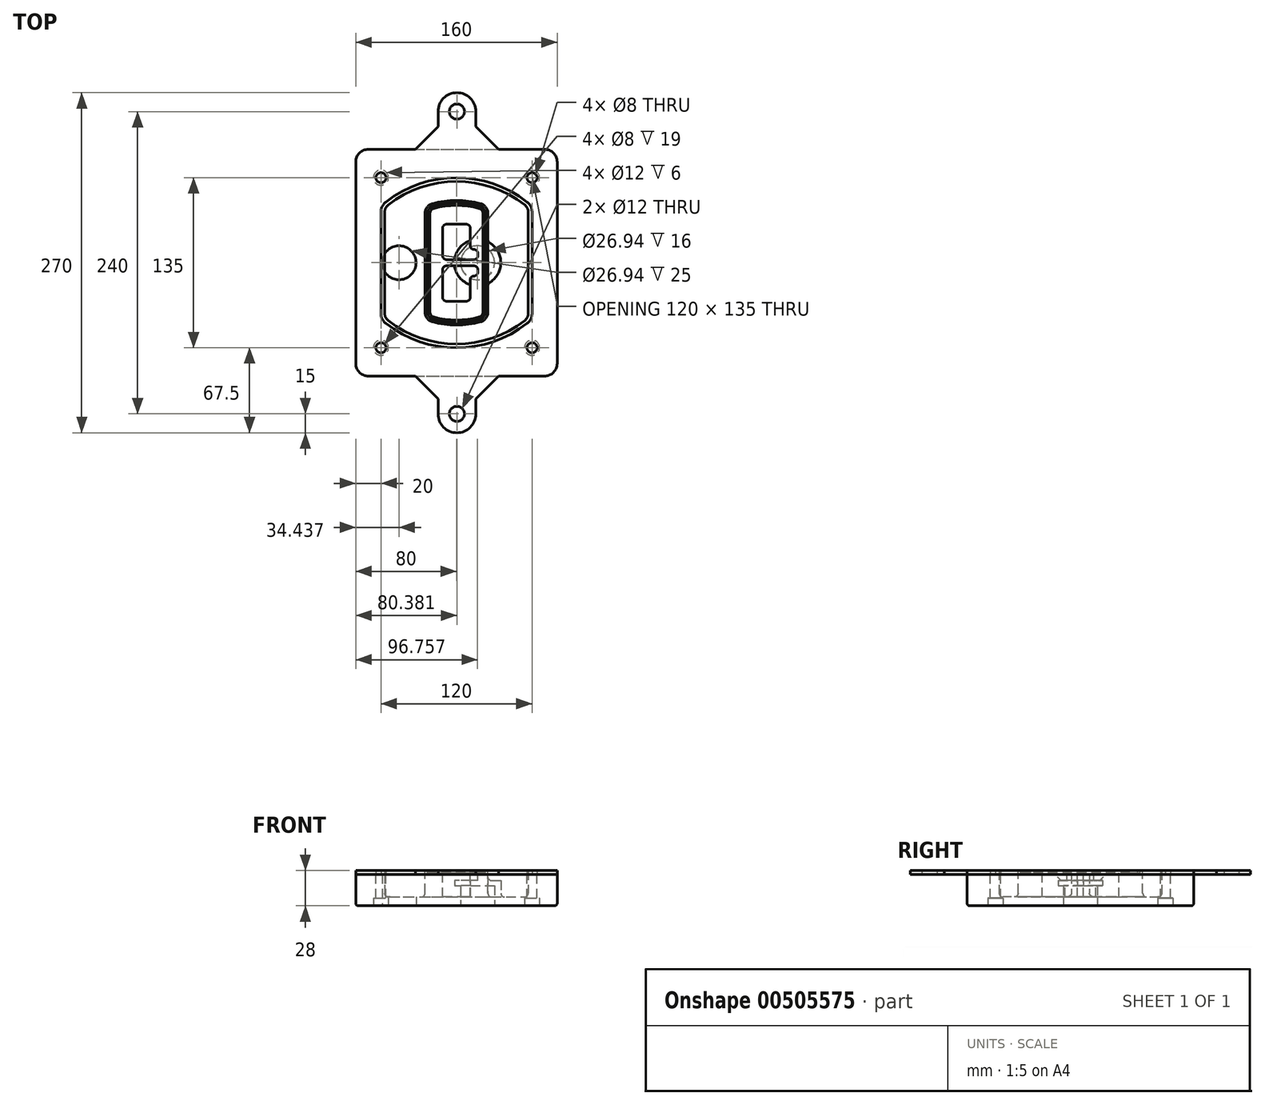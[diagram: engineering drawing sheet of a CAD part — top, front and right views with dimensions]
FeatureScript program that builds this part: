
annotation { "Feature Type Name" : "Feature", "Feature Type Description" : "" }
export const myFeature = defineFeature(function(context is Context, id is Id, definition is map)
    precondition{}
    {
        {
            var Q0;
            Q0=qCreatedBy(makeId("Top.planeOp"),FACE);
            var sketch = newSketch(context, id + "F0", { "sketchPlane" : qUnion([Q0])});
            skPoint(sketch, "E0.rect.middle", {"position": v(0, 0) * mm});
            skLineSegment(sketch, "E1.bottom", {"start": v(-70, -90) * mm, "end": v(70, -90) * mm});
            skLineSegment(sketch, "E1.top", {"start": v(-70, 90) * mm, "end": v(70, 90) * mm});
            skLineSegment(sketch, "E1.left", {"start": v(-80, -80) * mm, "end": v(-80, 80) * mm});
            skLineSegment(sketch, "E1.right", {"start": v(80, -80) * mm, "end": v(80, 80) * mm});
            skLineSegment(sketch, "E2", {"start": v(-80, 90) * mm, "end": v(80, -90) * mm, "construction": true});
            skLineSegment(sketch, "E3", {"start": v(80, 90) * mm, "end": v(-80, -90) * mm, "construction": true});
            skCircle(sketch, "E4", {"center": v(-60, 67.5) * mm, "radius": 4 * mm});
            skCircle(sketch, "E5", {"center": v(60, 67.5) * mm, "radius": 4 * mm});
            skCircle(sketch, "E6", {"center": v(60, -67.5) * mm, "radius": 4 * mm});
            skCircle(sketch, "E7", {"center": v(-60, -67.5) * mm, "radius": 4 * mm});
            skLineSegment(sketch, "E8", {"start": v(-60, 67.5) * mm, "end": v(60, 67.5) * mm, "construction": true});
            skLineSegment(sketch, "E9", {"start": v(60, 67.5) * mm, "end": v(60, -67.5) * mm, "construction": true});
            skLineSegment(sketch, "E10", {"start": v(60, -67.5) * mm, "end": v(-60, -67.5) * mm, "construction": true});
            skLineSegment(sketch, "E11", {"start": v(-60, -67.5) * mm, "end": v(-60, 67.5) * mm, "construction": true});
            skLineSegment(sketch, "E12", {"start": v(-60, 40.3) * mm, "end": v(-60, -40.3) * mm});
            skLineSegment(sketch, "E13", {"start": v(60, 40.3) * mm, "end": v(60, -40.3) * mm});
            skArc(sketch, "E14", {"start": v(56.15, 48.18) * mm, "mid": v(0, 67.5) * mm, "end": v(-56.15, 48.18) * mm});
            skArc(sketch, "E15", {"start": v(-56.15, -48.18) * mm, "mid": v(0, -67.5) * mm, "end": v(56.15, -48.18) * mm});
            skLineSegment(sketch, "E16", {"start": v(-60, 0) * mm, "end": v(60, 0) * mm, "construction": true});
            skPoint(sketch, "E17.visualSharp", {"position": v(-60, -45) * mm});
            skArc(sketch, "E17.filletArc", {"start": v(-60, -40.3) * mm, "mid": v(-58.99, -44.68) * mm, "end": v(-56.15, -48.18) * mm});
            skPoint(sketch, "E18.visualSharp", {"position": v(-60, 45) * mm});
            skArc(sketch, "E18.filletArc", {"start": v(-56.15, 48.18) * mm, "mid": v(-58.99, 44.68) * mm, "end": v(-60, 40.3) * mm});
            skPoint(sketch, "E19.visualSharp", {"position": v(60, 45) * mm});
            skArc(sketch, "E19.filletArc", {"start": v(60, 40.3) * mm, "mid": v(58.99, 44.68) * mm, "end": v(56.15, 48.18) * mm});
            skPoint(sketch, "E20.visualSharp", {"position": v(60, -45) * mm});
            skArc(sketch, "E20.filletArc", {"start": v(56.15, -48.18) * mm, "mid": v(58.99, -44.68) * mm, "end": v(60, -40.3) * mm});
            skPoint(sketch, "E21.visualSharp", {"position": v(-80, 90) * mm});
            skArc(sketch, "E21.filletArc", {"start": v(-70, 90) * mm, "mid": v(-77.07, 87.07) * mm, "end": v(-80, 80) * mm});
            skPoint(sketch, "E22.visualSharp", {"position": v(80, 90) * mm});
            skArc(sketch, "E22.filletArc", {"start": v(80, 80) * mm, "mid": v(77.07, 87.07) * mm, "end": v(70, 90) * mm});
            skPoint(sketch, "E23.visualSharp", {"position": v(80, -90) * mm});
            skArc(sketch, "E23.filletArc", {"start": v(70, -90) * mm, "mid": v(77.07, -87.07) * mm, "end": v(80, -80) * mm});
            skPoint(sketch, "E24.visualSharp", {"position": v(-80, -90) * mm});
            skArc(sketch, "E24.filletArc", {"start": v(-80, -80) * mm, "mid": v(-77.07, -87.07) * mm, "end": v(-70, -90) * mm});
            skArc(sketch, "E25.0", {"start": v(57, 40.3) * mm, "mid": v(56.3, 43.36) * mm, "end": v(54.3, 45.81) * mm});
            skLineSegment(sketch, "E25.1", {"start": v(57, 40.3) * mm, "end": v(57, -40.3) * mm});
            skArc(sketch, "E25.2", {"start": v(54.3, -45.81) * mm, "mid": v(56.3, -43.36) * mm, "end": v(57, -40.3) * mm});
            skArc(sketch, "E25.3", {"start": v(-54.3, -45.81) * mm, "mid": v(0, -64.5) * mm, "end": v(54.3, -45.81) * mm});
            skArc(sketch, "E25.4", {"start": v(-57, -40.3) * mm, "mid": v(-56.3, -43.36) * mm, "end": v(-54.3, -45.81) * mm});
            skArc(sketch, "E25.5", {"start": v(54.3, 45.81) * mm, "mid": v(0, 64.5) * mm, "end": v(-54.3, 45.81) * mm});
            skLineSegment(sketch, "E25.6", {"start": v(-57, 40.3) * mm, "end": v(-57, -40.3) * mm});
            skArc(sketch, "E25.7", {"start": v(-54.3, 45.81) * mm, "mid": v(-56.3, 43.36) * mm, "end": v(-57, 40.3) * mm});
            skArc(sketch, "E26.0", {"start": v(-58.62, 51.33) * mm, "mid": v(-62.58, 46.43) * mm, "end": v(-64, 40.3) * mm});
            skArc(sketch, "E26.1", {"start": v(58.62, 51.33) * mm, "mid": v(0, 71.5) * mm, "end": v(-58.62, 51.33) * mm});
            skArc(sketch, "E26.2", {"start": v(64, 40.3) * mm, "mid": v(62.58, 46.43) * mm, "end": v(58.62, 51.33) * mm});
            skLineSegment(sketch, "E26.3", {"start": v(64, 40.3) * mm, "end": v(64, -40.3) * mm});
            skArc(sketch, "E26.4", {"start": v(58.62, -51.33) * mm, "mid": v(62.58, -46.43) * mm, "end": v(64, -40.3) * mm});
            skLineSegment(sketch, "E26.5", {"start": v(-64, 40.3) * mm, "end": v(-64, -40.3) * mm});
            skArc(sketch, "E26.6", {"start": v(-58.62, -51.33) * mm, "mid": v(0, -71.5) * mm, "end": v(58.62, -51.33) * mm});
            skArc(sketch, "E26.7", {"start": v(-64, -40.3) * mm, "mid": v(-62.58, -46.43) * mm, "end": v(-58.62, -51.33) * mm});
            skSolve(sketch);
        }
        {
            var Q0;
            Q0=makeQuery(id+"F0.imprint","IMPRINT",FACE,{"disambiguationData":[TD([[makeQuery(id+"F0.imprint","IMPRINT",EDGE,{"derivedFrom":sQuery(id+"F0.wireOp",EDGE,"E1.bottom")}),1.0]])]});
            var Q1;
            Q1=makeQuery(id+"F0.imprint","IMPRINT",FACE,{"disambiguationData":[TD([[makeQuery(id+"F0.imprint","IMPRINT",EDGE,{"derivedFrom":sQuery(id+"F0.wireOp",EDGE,"E12")}),1.0]])]});
            var Q2;
            Q2=makeQuery(id+"F0.imprint","IMPRINT",FACE,{"disambiguationData":[TD([[makeQuery(id+"F0.imprint","IMPRINT",EDGE,{"derivedFrom":sQuery(id+"F0.wireOp",EDGE,"E25.0")}),1.0]])]});
            var Q3;
            Q3=makeQuery(id+"F0.imprint","IMPRINT",FACE,{"disambiguationData":[TD([[makeQuery(id+"F0.imprint","IMPRINT",EDGE,{"derivedFrom":sQuery(id+"F0.wireOp",EDGE,"E12")}),-1.0]])]});
            extrude(context, id + "F1", {"entities" : qUnion([Q0, Q1, Q2, Q3]), "oppositeDirection" : true, "depth" : 25 * mm});
        }
        {
            var Q0;
            Q0=makeQuery(id+"F0.imprint","IMPRINT",FACE,{"disambiguationData":[TD([[makeQuery(id+"F0.imprint","IMPRINT",EDGE,{"derivedFrom":sQuery(id+"F0.wireOp",EDGE,"E12")}),1.0]])]});
            extrude(context, id + "F2", {"entities" : qUnion([Q0]), "operationType" : NewBodyOperationType.ADD, "depth" : 3 * mm});
        }
        {
            var Q0;
            Q0=makeQuery(id+"F0.imprint","IMPRINT",FACE,{"disambiguationData":[TD([[makeQuery(id+"F0.imprint","IMPRINT",EDGE,{"derivedFrom":sQuery(id+"F0.wireOp",EDGE,"E25.0")}),1.0]])]});
            extrude(context, id + "F3", {"entities" : qUnion([Q0]), "operationType" : NewBodyOperationType.REMOVE, "oppositeDirection" : true, "depth" : 18 * mm});
        }
        {
            var Q0;
            Q0=makeQuery(id+"F2.opExtrude","CAP_FACE",FACE,{"disambiguationData":[OSD([sQuery(id+"F0.wireOp",EDGE,"E12"),sQuery(id+"F0.wireOp",EDGE,"E13"),sQuery(id+"F0.wireOp",EDGE,"E14"),sQuery(id+"F0.wireOp",EDGE,"E15"),sQuery(id+"F0.wireOp",EDGE,"E17.filletArc"),sQuery(id+"F0.wireOp",EDGE,"E18.filletArc"),sQuery(id+"F0.wireOp",EDGE,"E19.filletArc"),sQuery(id+"F0.wireOp",EDGE,"E20.filletArc"),sQuery(id+"F0.wireOp",EDGE,"E25.0"),sQuery(id+"F0.wireOp",EDGE,"E25.1"),sQuery(id+"F0.wireOp",EDGE,"E25.2"),sQuery(id+"F0.wireOp",EDGE,"E25.3"),sQuery(id+"F0.wireOp",EDGE,"E25.4"),sQuery(id+"F0.wireOp",EDGE,"E25.5"),sQuery(id+"F0.wireOp",EDGE,"E25.6"),sQuery(id+"F0.wireOp",EDGE,"E25.7")])],"isStart":false});
            var sketch = newSketch(context, id + "F4", { "sketchPlane" : qUnion([Q0])});
            skArc(sketch, "E27.0", {"start": v(-19.08, -46.97) * mm, "mid": v(0, -49.5) * mm, "end": v(19.08, -46.97) * mm});
            skArc(sketch, "E28.0", {"start": v(19.08, 46.97) * mm, "mid": v(0, 49.5) * mm, "end": v(-19.08, 46.97) * mm});
            skLineSegment(sketch, "E29", {"start": v(-25, 39.25) * mm, "end": v(-25, -39.25) * mm});
            skLineSegment(sketch, "E30", {"start": v(25, 39.25) * mm, "end": v(25, -39.25) * mm});
            skLineSegment(sketch, "E31", {"start": v(-25, 45.1) * mm, "end": v(25, 45.1) * mm, "construction": true});
            skLineSegment(sketch, "E32", {"start": v(-25, -45.1) * mm, "end": v(25, -45.1) * mm, "construction": true});
            skPoint(sketch, "E33.visualSharp", {"position": v(-25, 45.1) * mm});
            skArc(sketch, "E33.filletArc", {"start": v(-19.08, 46.97) * mm, "mid": v(-23.35, 44.11) * mm, "end": v(-25, 39.25) * mm});
            skPoint(sketch, "E34.visualSharp", {"position": v(25, 45.1) * mm});
            skArc(sketch, "E34.filletArc", {"start": v(25, 39.25) * mm, "mid": v(23.35, 44.11) * mm, "end": v(19.08, 46.97) * mm});
            skPoint(sketch, "E35.visualSharp", {"position": v(25, -45.1) * mm});
            skArc(sketch, "E35.filletArc", {"start": v(19.08, -46.97) * mm, "mid": v(23.35, -44.11) * mm, "end": v(25, -39.25) * mm});
            skPoint(sketch, "E36.visualSharp", {"position": v(-25, -45.1) * mm});
            skArc(sketch, "E36.filletArc", {"start": v(-25, -39.25) * mm, "mid": v(-23.35, -44.11) * mm, "end": v(-19.08, -46.97) * mm});
            skArc(sketch, "E37.0", {"start": v(54.3, 45.81) * mm, "mid": v(0, 64.5) * mm, "end": v(-54.3, 45.81) * mm});
            skArc(sketch, "E37.1", {"start": v(-54.3, 45.81) * mm, "mid": v(-56.3, 43.36) * mm, "end": v(-57, 40.3) * mm});
            skLineSegment(sketch, "E37.2", {"start": v(-57, 40.3) * mm, "end": v(-57, -40.3) * mm});
            skArc(sketch, "E37.3", {"start": v(-57, -40.3) * mm, "mid": v(-56.3, -43.36) * mm, "end": v(-54.3, -45.81) * mm});
            skArc(sketch, "E37.4", {"start": v(-54.3, -45.81) * mm, "mid": v(0, -64.5) * mm, "end": v(54.3, -45.81) * mm});
            skArc(sketch, "E37.5", {"start": v(54.3, -45.81) * mm, "mid": v(56.3, -43.36) * mm, "end": v(57, -40.3) * mm});
            skLineSegment(sketch, "E37.6", {"start": v(57, 40.3) * mm, "end": v(57, -40.3) * mm});
            skArc(sketch, "E37.7", {"start": v(57, 40.3) * mm, "mid": v(56.3, 43.36) * mm, "end": v(54.3, 45.81) * mm});
            skLineSegment(sketch, "E38.0", {"start": v(23, 39.25) * mm, "end": v(23, -39.25) * mm});
            skArc(sketch, "E38.1", {"start": v(18.56, -45.04) * mm, "mid": v(21.76, -42.9) * mm, "end": v(23, -39.25) * mm});
            skArc(sketch, "E38.2", {"start": v(-18.56, -45.04) * mm, "mid": v(0, -47.5) * mm, "end": v(18.56, -45.04) * mm});
            skArc(sketch, "E38.3", {"start": v(-23, -39.25) * mm, "mid": v(-21.76, -42.9) * mm, "end": v(-18.56, -45.04) * mm});
            skLineSegment(sketch, "E38.4", {"start": v(-23, 39.25) * mm, "end": v(-23, -39.25) * mm});
            skArc(sketch, "E38.5", {"start": v(23, 39.25) * mm, "mid": v(21.76, 42.9) * mm, "end": v(18.56, 45.04) * mm});
            skArc(sketch, "E38.6", {"start": v(-18.56, 45.04) * mm, "mid": v(-21.76, 42.9) * mm, "end": v(-23, 39.25) * mm});
            skArc(sketch, "E38.7", {"start": v(18.56, 45.04) * mm, "mid": v(0, 47.5) * mm, "end": v(-18.56, 45.04) * mm});
            skArc(sketch, "E39.0", {"start": v(21, 39.25) * mm, "mid": v(20.18, 41.68) * mm, "end": v(18.04, 43.1) * mm});
            skLineSegment(sketch, "E39.1", {"start": v(21, 39.25) * mm, "end": v(21, -39.25) * mm});
            skArc(sketch, "E39.2", {"start": v(18.04, -43.1) * mm, "mid": v(20.18, -41.68) * mm, "end": v(21, -39.25) * mm});
            skArc(sketch, "E39.3", {"start": v(-18.04, -43.1) * mm, "mid": v(0, -45.5) * mm, "end": v(18.04, -43.1) * mm});
            skArc(sketch, "E39.4", {"start": v(-21, -39.25) * mm, "mid": v(-20.18, -41.68) * mm, "end": v(-18.04, -43.1) * mm});
            skArc(sketch, "E39.5", {"start": v(18.04, 43.1) * mm, "mid": v(0, 45.5) * mm, "end": v(-18.04, 43.1) * mm});
            skLineSegment(sketch, "E39.6", {"start": v(-21, 39.25) * mm, "end": v(-21, -39.25) * mm});
            skArc(sketch, "E39.7", {"start": v(-18.04, 43.1) * mm, "mid": v(-20.18, 41.68) * mm, "end": v(-21, 39.25) * mm});
            skLineSegment(sketch, "E40", {"start": v(-25, 0) * mm, "end": v(25, 0) * mm, "construction": true});
            skLineSegment(sketch, "E41", {"start": v(-11, 5.5) * mm, "end": v(-11, 27.5) * mm});
            skLineSegment(sketch, "E42", {"start": v(-8, 30.5) * mm, "end": v(8, 30.5) * mm});
            skLineSegment(sketch, "E43", {"start": v(11, 27.5) * mm, "end": v(11, 13.5) * mm});
            skLineSegment(sketch, "E44", {"start": v(14, 10.5) * mm, "end": v(14, 10.5) * mm});
            skLineSegment(sketch, "E45", {"start": v(17, 7.5) * mm, "end": v(17, 5.5) * mm});
            skLineSegment(sketch, "E46", {"start": v(14, 2.5) * mm, "end": v(-8, 2.5) * mm});
            skPoint(sketch, "E47.visualSharp", {"position": v(-11, 30.5) * mm});
            skArc(sketch, "E47.filletArc", {"start": v(-8, 30.5) * mm, "mid": v(-10.12, 29.62) * mm, "end": v(-11, 27.5) * mm});
            skPoint(sketch, "E48.visualSharp", {"position": v(11, 30.5) * mm});
            skArc(sketch, "E48.filletArc", {"start": v(11, 27.5) * mm, "mid": v(10.12, 29.62) * mm, "end": v(8, 30.5) * mm});
            skPoint(sketch, "E49.visualSharp", {"position": v(11, 10.5) * mm});
            skArc(sketch, "E49.filletArc", {"start": v(11, 13.5) * mm, "mid": v(11.88, 11.38) * mm, "end": v(14, 10.5) * mm});
            skPoint(sketch, "E50.visualSharp", {"position": v(17, 10.5) * mm});
            skArc(sketch, "E50.filletArc", {"start": v(17, 7.5) * mm, "mid": v(16.12, 9.62) * mm, "end": v(14, 10.5) * mm});
            skPoint(sketch, "E51.visualSharp", {"position": v(17, 2.5) * mm});
            skArc(sketch, "E51.filletArc", {"start": v(14, 2.5) * mm, "mid": v(16.12, 3.38) * mm, "end": v(17, 5.5) * mm});
            skPoint(sketch, "E52.visualSharp", {"position": v(-11, 2.5) * mm});
            skArc(sketch, "E52.filletArc", {"start": v(-11, 5.5) * mm, "mid": v(-10.12, 3.38) * mm, "end": v(-8, 2.5) * mm});
            skLineSegment(sketch, "E53.0.MirrorCS", {"start": v(14, -2.5) * mm, "end": v(-8, -2.5) * mm});
            skArc(sketch, "E54.0.MirrorCS", {"start": v(-11, -5.5) * mm, "mid": v(-10.12, -3.38) * mm, "end": v(-8, -2.5) * mm});
            skLineSegment(sketch, "E55.0.MirrorCS", {"start": v(-11, -5.5) * mm, "end": v(-11, -27.5) * mm});
            skArc(sketch, "E56.0.MirrorCS", {"start": v(-8, -30.5) * mm, "mid": v(-10.12, -29.62) * mm, "end": v(-11, -27.5) * mm});
            skLineSegment(sketch, "E57.0.MirrorCS", {"start": v(-8, -30.5) * mm, "end": v(8, -30.5) * mm});
            skArc(sketch, "E58.0.MirrorCS", {"start": v(11, -27.5) * mm, "mid": v(10.12, -29.62) * mm, "end": v(8, -30.5) * mm});
            skLineSegment(sketch, "E59.0.MirrorCS", {"start": v(11, -27.5) * mm, "end": v(11, -13.5) * mm});
            skArc(sketch, "E60.0.MirrorCS", {"start": v(11, -13.5) * mm, "mid": v(11.88, -11.38) * mm, "end": v(14, -10.5) * mm});
            skArc(sketch, "E61.0.MirrorCS", {"start": v(17, -7.5) * mm, "mid": v(16.12, -9.62) * mm, "end": v(14, -10.5) * mm});
            skLineSegment(sketch, "E62.0.MirrorCS", {"start": v(17, -7.5) * mm, "end": v(17, -5.5) * mm});
            skArc(sketch, "E63.0.MirrorCS", {"start": v(14, -2.5) * mm, "mid": v(16.12, -3.38) * mm, "end": v(17, -5.5) * mm});
            skSolve(sketch);
        }
        {
            var Q0;
            Q0=makeQuery(id+"F4.imprint","IMPRINT",FACE,{"disambiguationData":[TD([[makeQuery(id+"F4.imprint","IMPRINT",EDGE,{"derivedFrom":sQuery(id+"F4.wireOp",EDGE,"E27.0")}),1.0]])]});
            var Q1;
            Q1=makeQuery(id+"F4.imprint","IMPRINT",FACE,{"disambiguationData":[TD([[makeQuery(id+"F4.imprint","IMPRINT",EDGE,{"derivedFrom":sQuery(id+"F4.wireOp",EDGE,"E38.0")}),-1.0]])]});
            var Q2;
            Q2=makeQuery(id+"F4.imprint","IMPRINT",FACE,{"disambiguationData":[TD([[makeQuery(id+"F4.imprint","IMPRINT",EDGE,{"derivedFrom":sQuery(id+"F4.wireOp",EDGE,"E39.0")}),1.0]])]});
            extrude(context, id + "F5", {"entities" : qUnion([Q0, Q1, Q2]), "operationType" : NewBodyOperationType.ADD, "endBound" : BoundingType.UP_TO_NEXT, "oppositeDirection" : true, "depth" : 25 * mm});
        }
        {
            var Q0;
            Q0=makeQuery(id+"F4.imprint","IMPRINT",FACE,{"disambiguationData":[TD([[makeQuery(id+"F4.imprint","IMPRINT",EDGE,{"derivedFrom":sQuery(id+"F4.wireOp",EDGE,"E38.0")}),-1.0]])]});
            extrude(context, id + "F6", {"entities" : qUnion([Q0]), "operationType" : NewBodyOperationType.REMOVE, "oppositeDirection" : true, "depth" : 2 * mm});
        }
        {
            var Q0;
            Q0=makeQuery(id+"F1.opExtrude","CAP_FACE",FACE,{"disambiguationData":[OSD([sQuery(id+"F0.wireOp",EDGE,"E1.bottom"),sQuery(id+"F0.wireOp",EDGE,"E1.top"),sQuery(id+"F0.wireOp",EDGE,"E1.left"),sQuery(id+"F0.wireOp",EDGE,"E1.right"),sQuery(id+"F0.wireOp",EDGE,"E4"),sQuery(id+"F0.wireOp",EDGE,"E5"),sQuery(id+"F0.wireOp",EDGE,"E6"),sQuery(id+"F0.wireOp",EDGE,"E7"),sQuery(id+"F0.wireOp",EDGE,"E21.filletArc"),sQuery(id+"F0.wireOp",EDGE,"E22.filletArc"),sQuery(id+"F0.wireOp",EDGE,"E23.filletArc"),sQuery(id+"F0.wireOp",EDGE,"E24.filletArc")])],"isStart":false});
            var sketch = newSketch(context, id + "F7", { "sketchPlane" : qUnion([Q0])});
            skCircle(sketch, "E64", {"center": v(16.76, 0) * mm, "radius": 13.47 * mm});
            skCircle(sketch, "E65", {"center": v(-45.56, 0) * mm, "radius": 13.47 * mm});
            skLineSegment(sketch, "E66", {"start": v(80, 0) * mm, "end": v(-80, 0) * mm});
            skCircle(sketch, "E67", {"center": v(16.76, 0) * mm, "radius": 18.47 * mm});
            skCircle(sketch, "E68", {"center": v(60, -67.5) * mm, "radius": 6 * mm});
            skCircle(sketch, "E69", {"center": v(-60, -67.5) * mm, "radius": 6 * mm});
            skCircle(sketch, "E70", {"center": v(-60, 67.5) * mm, "radius": 6 * mm});
            skCircle(sketch, "E71", {"center": v(60, 67.5) * mm, "radius": 6 * mm});
            skSolve(sketch);
        }
        {
            var Q0;
            {var subQ1=sQuery(id+"F7.wireOp",EDGE,"E66");var subQ4=sQuery(id+"F7.wireOp",EDGE,"E64");var subQ6=makeQuery(id+"F7.imprint","INTERSECT",VERTEX,{"disambiguationData":[OD(0.0)],"derivedFrom":[subQ4,subQ1]});Q0=makeQuery(id+"F7.imprint","IMPRINT",FACE,{"disambiguationData":[TD([[makeQuery(id+"F7.imprint","IMPRINT",EDGE,{"disambiguationData":[TD([[subQ6,-1.0]])],"derivedFrom":subQ4}),-1.0]])]});}
            var Q1;
            {var subQ0=sQuery(id+"F7.wireOp",EDGE,"E66");var subQ1=sQuery(id+"F7.wireOp",EDGE,"E64");var subQ3=makeQuery(id+"F7.imprint","INTERSECT",VERTEX,{"disambiguationData":[OD(0.0)],"derivedFrom":[subQ1,subQ0]});Q1=makeQuery(id+"F7.imprint","IMPRINT",FACE,{"disambiguationData":[TD([[makeQuery(id+"F7.imprint","IMPRINT",EDGE,{"disambiguationData":[TD([[subQ3,-1.0]])],"derivedFrom":subQ1}),1.0]])]});}
            var Q2;
            {var subQ0=sQuery(id+"F7.wireOp",EDGE,"E66");var subQ1=sQuery(id+"F7.wireOp",EDGE,"E64");var subQ3=makeQuery(id+"F7.imprint","INTERSECT",VERTEX,{"disambiguationData":[OD(0.0)],"derivedFrom":[subQ1,subQ0]});Q2=makeQuery(id+"F7.imprint","IMPRINT",FACE,{"disambiguationData":[TD([[makeQuery(id+"F7.imprint","IMPRINT",EDGE,{"disambiguationData":[TD([[subQ3,1.0]])],"derivedFrom":subQ1}),1.0]])]});}
            var Q3;
            {var subQ1=sQuery(id+"F7.wireOp",EDGE,"E66");var subQ4=sQuery(id+"F7.wireOp",EDGE,"E64");var subQ6=makeQuery(id+"F7.imprint","INTERSECT",VERTEX,{"disambiguationData":[OD(0.0)],"derivedFrom":[subQ4,subQ1]});Q3=makeQuery(id+"F7.imprint","IMPRINT",FACE,{"disambiguationData":[TD([[makeQuery(id+"F7.imprint","IMPRINT",EDGE,{"disambiguationData":[TD([[subQ6,1.0]])],"derivedFrom":subQ4}),-1.0]])]});}
            extrude(context, id + "F8", {"entities" : qUnion([Q0, Q1, Q2, Q3]), "operationType" : NewBodyOperationType.ADD, "oppositeDirection" : true, "depth" : 20 * mm});
        }
        {
            var Q0;
            {var subQ0=sQuery(id+"F7.wireOp",EDGE,"E66");var subQ1=sQuery(id+"F7.wireOp",EDGE,"E64");var subQ3=makeQuery(id+"F7.imprint","INTERSECT",VERTEX,{"disambiguationData":[OD(0.0)],"derivedFrom":[subQ1,subQ0]});Q0=makeQuery(id+"F7.imprint","IMPRINT",FACE,{"disambiguationData":[TD([[makeQuery(id+"F7.imprint","IMPRINT",EDGE,{"disambiguationData":[TD([[subQ3,-1.0]])],"derivedFrom":subQ1}),1.0]])]});}
            var Q1;
            {var subQ0=sQuery(id+"F7.wireOp",EDGE,"E66");var subQ1=sQuery(id+"F7.wireOp",EDGE,"E64");var subQ3=makeQuery(id+"F7.imprint","INTERSECT",VERTEX,{"disambiguationData":[OD(0.0)],"derivedFrom":[subQ1,subQ0]});Q1=makeQuery(id+"F7.imprint","IMPRINT",FACE,{"disambiguationData":[TD([[makeQuery(id+"F7.imprint","IMPRINT",EDGE,{"disambiguationData":[TD([[subQ3,1.0]])],"derivedFrom":subQ1}),1.0]])]});}
            extrude(context, id + "F9", {"entities" : qUnion([Q0, Q1]), "operationType" : NewBodyOperationType.REMOVE, "oppositeDirection" : true, "depth" : 16 * mm});
        }
        {
            var Q0;
            {var subQ0=sQuery(id+"F7.wireOp",EDGE,"E66");var subQ1=sQuery(id+"F7.wireOp",EDGE,"E65");var subQ3=makeQuery(id+"F7.imprint","INTERSECT",VERTEX,{"disambiguationData":[OD(0.0)],"derivedFrom":[subQ1,subQ0]});Q0=makeQuery(id+"F7.imprint","IMPRINT",FACE,{"disambiguationData":[TD([[makeQuery(id+"F7.imprint","IMPRINT",EDGE,{"disambiguationData":[TD([[subQ3,-1.0]])],"derivedFrom":subQ1}),1.0]])]});}
            var Q1;
            {var subQ0=sQuery(id+"F7.wireOp",EDGE,"E66");var subQ1=sQuery(id+"F7.wireOp",EDGE,"E65");var subQ3=makeQuery(id+"F7.imprint","INTERSECT",VERTEX,{"disambiguationData":[OD(0.0)],"derivedFrom":[subQ1,subQ0]});Q1=makeQuery(id+"F7.imprint","IMPRINT",FACE,{"disambiguationData":[TD([[makeQuery(id+"F7.imprint","IMPRINT",EDGE,{"disambiguationData":[TD([[subQ3,1.0]])],"derivedFrom":subQ1}),1.0]])]});}
            extrude(context, id + "F10", {"entities" : qUnion([Q0, Q1]), "operationType" : NewBodyOperationType.REMOVE, "oppositeDirection" : true, "depth" : 25 * mm});
        }
        {
            var Q0;
            Q0=makeQuery(id+"F7.imprint","IMPRINT",FACE,{"disambiguationData":[TD([[makeQuery(id+"F7.imprint","IMPRINT",EDGE,{"derivedFrom":sQuery(id+"F7.wireOp",EDGE,"E68")}),1.0]])]});
            var Q1;
            Q1=makeQuery(id+"F7.imprint","IMPRINT",FACE,{"disambiguationData":[TD([[makeQuery(id+"F7.imprint","IMPRINT",EDGE,{"derivedFrom":makeQuery(id+"F1.opExtrude","CAP_EDGE",EDGE,{"disambiguationData":[OSD([sQuery(id+"F0.wireOp",EDGE,"E5")])],"isStart":false})}),-1.0]])]});
            var Q2;
            Q2=makeQuery(id+"F7.imprint","IMPRINT",FACE,{"disambiguationData":[TD([[makeQuery(id+"F7.imprint","IMPRINT",EDGE,{"derivedFrom":sQuery(id+"F7.wireOp",EDGE,"E69")}),1.0]])]});
            var Q3;
            Q3=makeQuery(id+"F7.imprint","IMPRINT",FACE,{"disambiguationData":[TD([[makeQuery(id+"F7.imprint","IMPRINT",EDGE,{"derivedFrom":makeQuery(id+"F1.opExtrude","CAP_EDGE",EDGE,{"disambiguationData":[OSD([sQuery(id+"F0.wireOp",EDGE,"E4")])],"isStart":false})}),-1.0]])]});
            var Q4;
            Q4=makeQuery(id+"F7.imprint","IMPRINT",FACE,{"disambiguationData":[TD([[makeQuery(id+"F7.imprint","IMPRINT",EDGE,{"derivedFrom":sQuery(id+"F7.wireOp",EDGE,"E70")}),1.0]])]});
            var Q5;
            Q5=makeQuery(id+"F7.imprint","IMPRINT",FACE,{"disambiguationData":[TD([[makeQuery(id+"F7.imprint","IMPRINT",EDGE,{"derivedFrom":makeQuery(id+"F1.opExtrude","CAP_EDGE",EDGE,{"disambiguationData":[OSD([sQuery(id+"F0.wireOp",EDGE,"E7")])],"isStart":false})}),-1.0]])]});
            var Q6;
            Q6=makeQuery(id+"F7.imprint","IMPRINT",FACE,{"disambiguationData":[TD([[makeQuery(id+"F7.imprint","IMPRINT",EDGE,{"derivedFrom":sQuery(id+"F7.wireOp",EDGE,"E71")}),1.0]])]});
            var Q7;
            Q7=makeQuery(id+"F7.imprint","IMPRINT",FACE,{"disambiguationData":[TD([[makeQuery(id+"F7.imprint","IMPRINT",EDGE,{"derivedFrom":makeQuery(id+"F1.opExtrude","CAP_EDGE",EDGE,{"disambiguationData":[OSD([sQuery(id+"F0.wireOp",EDGE,"E6")])],"isStart":false})}),-1.0]])]});
            extrude(context, id + "F11", {"entities" : qUnion([Q0, Q1, Q2, Q3, Q4, Q5, Q6, Q7]), "operationType" : NewBodyOperationType.REMOVE, "oppositeDirection" : true, "depth" : 6 * mm});
        }
        {
            var Q0;
            Q0=makeQuery(id+"F9.boolean.opBoolean","COPY",FACE,{"derivedFrom":makeQuery(id+"F9.opExtrude","CAP_FACE",FACE,{"disambiguationData":[OSD([sQuery(id+"F7.wireOp",EDGE,"E64")])],"isStart":false})});
            var sketch = newSketch(context, id + "F12", { "sketchPlane" : qUnion([Q0])});
            skArc(sketch, "E72.0", {"start": v(11, 17.55) * mm, "mid": v(2.57, 11.82) * mm, "end": v(-1.54, 2.5) * mm});
            skArc(sketch, "E72.1", {"start": v(-1.54, -2.5) * mm, "mid": v(2.57, -11.82) * mm, "end": v(11, -17.55) * mm});
            skLineSegment(sketch, "E73", {"start": v(-1.54, -2.5) * mm, "end": v(14, -2.5) * mm});
            skLineSegment(sketch, "E74.0", {"start": v(14, 2.5) * mm, "end": v(-1.54, 2.5) * mm});
            skArc(sketch, "E74.1", {"start": v(14, 2.5) * mm, "mid": v(16.12, 3.38) * mm, "end": v(17, 5.5) * mm});
            skLineSegment(sketch, "E74.2", {"start": v(17, 7.5) * mm, "end": v(17, 5.5) * mm});
            skArc(sketch, "E74.3", {"start": v(17, 7.5) * mm, "mid": v(16.12, 9.62) * mm, "end": v(14, 10.5) * mm});
            skArc(sketch, "E74.4", {"start": v(11, 13.5) * mm, "mid": v(11.88, 11.38) * mm, "end": v(14, 10.5) * mm});
            skLineSegment(sketch, "E74.5", {"start": v(11, 17.55) * mm, "end": v(11, 13.5) * mm});
            skLineSegment(sketch, "E74.7", {"start": v(14, -2.5) * mm, "end": v(-1.54, -2.5) * mm});
            skArc(sketch, "E74.8", {"start": v(14, -2.5) * mm, "mid": v(16.12, -3.38) * mm, "end": v(17, -5.5) * mm});
            skLineSegment(sketch, "E74.9", {"start": v(17, -7.5) * mm, "end": v(17, -5.5) * mm});
            skArc(sketch, "E74.10", {"start": v(17, -7.5) * mm, "mid": v(16.12, -9.62) * mm, "end": v(14, -10.5) * mm});
            skArc(sketch, "E74.11", {"start": v(11, -13.5) * mm, "mid": v(11.88, -11.38) * mm, "end": v(14, -10.5) * mm});
            skLineSegment(sketch, "E74.12", {"start": v(11, -17.55) * mm, "end": v(11, -13.5) * mm});
            skPoint(sketch, "E75.orphan", {"position": v(11, -27.5) * mm});
            skPoint(sketch, "E76.orphan", {"position": v(-8, -2.5) * mm});
            skPoint(sketch, "E77.orphan", {"position": v(-8, 2.5) * mm});
            skPoint(sketch, "E78.orphan", {"position": v(11, 27.5) * mm});
            skSolve(sketch);
        }
        {
            var Q0;
            {var subQ7=sQuery(id+"F12.wireOp",EDGE,"E72.0");var subQ14=sQuery(id+"F12.wireOp",EDGE,"E72.1");var subQ16=sQuery(id+"F12.wireOp",EDGE,"E74.1");var subQ18=sQuery(id+"F12.wireOp",EDGE,"E74.8");Q0=qUnion([makeQuery(id+"F12.imprint","IMPRINT",FACE,{"disambiguationData":[TD([[makeQuery(id+"F12.imprint","IMPRINT",EDGE,{"derivedFrom":subQ7}),1.0]])]}),makeQuery(id+"F12.imprint","IMPRINT",FACE,{"disambiguationData":[TD([[makeQuery(id+"F12.imprint","IMPRINT",EDGE,{"derivedFrom":subQ14}),1.0]])]}),makeQuery(id+"F12.imprint","IMPRINT",FACE,{"disambiguationData":[TD([[makeQuery(id+"F12.imprint","IMPRINT",EDGE,{"derivedFrom":subQ16}),1.0]])]}),makeQuery(id+"F12.imprint","IMPRINT",FACE,{"disambiguationData":[TD([[makeQuery(id+"F12.imprint","IMPRINT",EDGE,{"derivedFrom":subQ18}),-1.0]])]})]);}
            var Q1;
            Q1=makeQuery(id+"F5.boolean.opBoolean","SPLIT",FACE,{"disambiguationData":[TD([makeQuery(id+"F5.opExtrude","SWEPT_FACE",FACE,{"disambiguationData":[OSD([sQuery(id+"F4.wireOp",EDGE,"E41")])]})])],"derivedFrom":makeQuery(id+"F3.boolean.opBoolean","COPY",FACE,{"derivedFrom":makeQuery(id+"F3.opExtrude","CAP_FACE",FACE,{"disambiguationData":[OSD([sQuery(id+"F0.wireOp",EDGE,"E25.0"),sQuery(id+"F0.wireOp",EDGE,"E25.1"),sQuery(id+"F0.wireOp",EDGE,"E25.2"),sQuery(id+"F0.wireOp",EDGE,"E25.3"),sQuery(id+"F0.wireOp",EDGE,"E25.4"),sQuery(id+"F0.wireOp",EDGE,"E25.5"),sQuery(id+"F0.wireOp",EDGE,"E25.6"),sQuery(id+"F0.wireOp",EDGE,"E25.7")])],"isStart":false})})});
            extrude(context, id + "F13", {"entities" : qUnion([Q0]), "operationType" : NewBodyOperationType.REMOVE, "endBound" : BoundingType.UP_TO_SURFACE, "endBoundEntityFace" : qUnion([Q1]), "depth" : 25 * mm});
        }
        {
            var Q0;
            Q0=makeQuery(id+"F3.boolean.opBoolean","COPY",EDGE,{"derivedFrom":makeQuery(id+"F3.opExtrude","CAP_EDGE",EDGE,{"disambiguationData":[OSD([sQuery(id+"F0.wireOp",EDGE,"E25.6")])],"isStart":false})});
            var Q1;
            Q1=makeQuery(id+"F8.boolean.opBoolean","INTERSECT",EDGE,{"derivedFrom":[makeQuery(id+"F5.opExtrude","SWEPT_FACE",FACE,{"disambiguationData":[OSD([sQuery(id+"F4.wireOp",EDGE,"E30")])]}),makeQuery(id+"F8.opExtrude","CAP_FACE",FACE,{"disambiguationData":[OSD([sQuery(id+"F7.wireOp",EDGE,"E67")])],"isStart":false})]});
            var Q2;
            Q2=makeQuery(id+"F8.boolean.opBoolean","INTERSECT",EDGE,{"disambiguationData":[OD(1.0)],"derivedFrom":[makeQuery(id+"F5.opExtrude","SWEPT_FACE",FACE,{"disambiguationData":[OSD([sQuery(id+"F4.wireOp",EDGE,"E30")])]}),makeQuery(id+"F8.opExtrude","SWEPT_FACE",FACE,{"disambiguationData":[OSD([sQuery(id+"F7.wireOp",EDGE,"E67")])]})]});
            var Q3;
            {var subQ0=sQuery(id+"F4.wireOp",EDGE,"E30");Q3=makeQuery(id+"F8.boolean.opBoolean","SPLIT",EDGE,{"disambiguationData":[TD([makeQuery(id+"F5.opExtrude","SWEPT_FACE",FACE,{"disambiguationData":[OSD([sQuery(id+"F4.wireOp",EDGE,"E35.filletArc")])]})])],"derivedFrom":makeQuery(id+"F5.opExtrude","CAP_EDGE",EDGE,{"disambiguationData":[OSD([subQ0])],"isStart":false})});}
            var Q4;
            {var subQ0=sQuery(id+"F0.wireOp",EDGE,"E25.7");var subQ1=sQuery(id+"F0.wireOp",EDGE,"E25.1");var subQ2=sQuery(id+"F0.wireOp",EDGE,"E25.6");var subQ3=sQuery(id+"F0.wireOp",EDGE,"E25.5");var subQ4=sQuery(id+"F0.wireOp",EDGE,"E25.4");var subQ5=sQuery(id+"F0.wireOp",EDGE,"E25.0");var subQ6=sQuery(id+"F0.wireOp",EDGE,"E25.2");var subQ7=sQuery(id+"F0.wireOp",EDGE,"E25.3");Q4=makeQuery(id+"F8.boolean.opBoolean","INTERSECT",EDGE,{"derivedFrom":[makeQuery(id+"F5.boolean.opBoolean","SPLIT",FACE,{"disambiguationData":[TD([makeQuery(id+"F2.opExtrude","SWEPT_FACE",FACE,{"disambiguationData":[OSD([subQ5])]})])],"derivedFrom":makeQuery(id+"F3.boolean.opBoolean","COPY",FACE,{"derivedFrom":makeQuery(id+"F3.opExtrude","CAP_FACE",FACE,{"disambiguationData":[OSD([subQ5,subQ1,subQ6,subQ7,subQ4,subQ3,subQ2,subQ0])],"isStart":false})})}),makeQuery(id+"F8.opExtrude","SWEPT_FACE",FACE,{"disambiguationData":[OSD([sQuery(id+"F7.wireOp",EDGE,"E67")])]})]});}
            var Q5;
            Q5=makeQuery(id+"F8.boolean.opBoolean","INTERSECT",EDGE,{"disambiguationData":[OD(0.0)],"derivedFrom":[makeQuery(id+"F5.opExtrude","SWEPT_FACE",FACE,{"disambiguationData":[OSD([sQuery(id+"F4.wireOp",EDGE,"E30")])]}),makeQuery(id+"F8.opExtrude","SWEPT_FACE",FACE,{"disambiguationData":[OSD([sQuery(id+"F7.wireOp",EDGE,"E67")])]})]});
            fillet(context, id + "F14", {"entities" : qUnion([Q0, Q1, Q2, Q3, Q4, Q5]), "radius" : 3 * mm, "tangentPropagation" : true, "allowEdgeOverflow" : false});
        }
        {
            var Q0;
            Q0=makeQuery(id+"F1.opExtrude","CAP_EDGE",EDGE,{"disambiguationData":[OSD([sQuery(id+"F0.wireOp",EDGE,"E1.bottom")])],"isStart":false});
            fillet(context, id + "F15", {"entities" : qUnion([Q0]), "radius" : 2 * mm, "tangentPropagation" : true, "allowEdgeOverflow" : false});
        }
        {
            var Q0;
            {var subQ0=sQuery(id+"F0.wireOp",EDGE,"E21.filletArc");var subQ1=sQuery(id+"F0.wireOp",EDGE,"E7");var subQ2=sQuery(id+"F0.wireOp",EDGE,"E6");var subQ3=sQuery(id+"F0.wireOp",EDGE,"E5");var subQ4=sQuery(id+"F0.wireOp",EDGE,"E4");var subQ5=sQuery(id+"F0.wireOp",EDGE,"E22.filletArc");var subQ6=sQuery(id+"F0.wireOp",EDGE,"E1.bottom");var subQ7=sQuery(id+"F0.wireOp",EDGE,"E1.right");var subQ8=sQuery(id+"F0.wireOp",EDGE,"E1.top");var subQ9=sQuery(id+"F0.wireOp",EDGE,"E1.left");var subQ10=sQuery(id+"F0.wireOp",EDGE,"E23.filletArc");var subQ11=sQuery(id+"F0.wireOp",EDGE,"E24.filletArc");Q0=makeQuery(id+"F2.boolean.opBoolean","SPLIT",FACE,{"disambiguationData":[TD([makeQuery(id+"F1.opExtrude","SWEPT_FACE",FACE,{"disambiguationData":[OSD([subQ6])]})])],"derivedFrom":makeQuery(id+"F1.opExtrude","CAP_FACE",FACE,{"disambiguationData":[OSD([subQ6,subQ8,subQ9,subQ7,subQ4,subQ3,subQ2,subQ1,subQ0,subQ5,subQ10,subQ11])],"isStart":true})});}
            var sketch = newSketch(context, id + "F16", { "sketchPlane" : qUnion([Q0])});
            skLineSegment(sketch, "E79.0", {"start": v(-70, 90) * mm, "end": v(70, 90) * mm});
            skArc(sketch, "E79.1", {"start": v(-70, 90) * mm, "mid": v(-77.07, 87.07) * mm, "end": v(-80, 80) * mm});
            skLineSegment(sketch, "E79.2", {"start": v(-80, -80) * mm, "end": v(-80, 80) * mm});
            skArc(sketch, "E79.3", {"start": v(-80, -80) * mm, "mid": v(-77.07, -87.07) * mm, "end": v(-70, -90) * mm});
            skLineSegment(sketch, "E79.4", {"start": v(-70, -90) * mm, "end": v(70, -90) * mm});
            skArc(sketch, "E79.5", {"start": v(70, -90) * mm, "mid": v(77.07, -87.07) * mm, "end": v(80, -80) * mm});
            skLineSegment(sketch, "E79.6", {"start": v(80, -80) * mm, "end": v(80, 80) * mm});
            skArc(sketch, "E79.7", {"start": v(80, 80) * mm, "mid": v(77.07, 87.07) * mm, "end": v(70, 90) * mm});
            skArc(sketch, "E79.8", {"start": v(56.15, 48.18) * mm, "mid": v(0, 67.5) * mm, "end": v(-56.15, 48.18) * mm});
            skArc(sketch, "E79.9", {"start": v(-56.15, 48.18) * mm, "mid": v(-58.99, 44.68) * mm, "end": v(-60, 40.3) * mm});
            skLineSegment(sketch, "E79.10", {"start": v(-60, 40.3) * mm, "end": v(-60, -40.3) * mm});
            skArc(sketch, "E79.11", {"start": v(-60, -40.3) * mm, "mid": v(-58.99, -44.68) * mm, "end": v(-56.15, -48.18) * mm});
            skArc(sketch, "E79.12", {"start": v(-56.15, -48.18) * mm, "mid": v(0, -67.5) * mm, "end": v(56.15, -48.18) * mm});
            skArc(sketch, "E79.13", {"start": v(56.15, -48.18) * mm, "mid": v(58.99, -44.68) * mm, "end": v(60, -40.3) * mm});
            skLineSegment(sketch, "E79.14", {"start": v(60, 40.3) * mm, "end": v(60, -40.3) * mm});
            skArc(sketch, "E79.15", {"start": v(60, 40.3) * mm, "mid": v(58.99, 44.68) * mm, "end": v(56.15, 48.18) * mm});
            skCircle(sketch, "E79.16", {"center": v(-60, 67.5) * mm, "radius": 4 * mm});
            skCircle(sketch, "E79.17", {"center": v(60, 67.5) * mm, "radius": 4 * mm});
            skCircle(sketch, "E79.18", {"center": v(-60, -67.5) * mm, "radius": 4 * mm});
            skCircle(sketch, "E79.19", {"center": v(60, -67.5) * mm, "radius": 4 * mm});
            skLineSegment(sketch, "E80", {"start": v(-14.62, 108) * mm, "end": v(-14.62, 120) * mm});
            skLineSegment(sketch, "E81", {"start": v(15.38, 120) * mm, "end": v(15.38, 108) * mm});
            skArc(sketch, "E82", {"start": v(15.38, 120) * mm, "mid": v(0.38, 135) * mm, "end": v(-14.62, 120) * mm});
            skLineSegment(sketch, "E83", {"start": v(0.38, 120) * mm, "end": v(0.38, 90) * mm, "construction": true});
            skCircle(sketch, "E84", {"center": v(0.38, 120) * mm, "radius": 6 * mm});
            skLineSegment(sketch, "E85", {"start": v(15.38, 108) * mm, "end": v(33.38, 90) * mm});
            skLineSegment(sketch, "E86", {"start": v(-14.62, 108) * mm, "end": v(-32.62, 90) * mm});
            skLineSegment(sketch, "E87", {"start": v(-80, 0) * mm, "end": v(80, 0) * mm, "construction": true});
            skLineSegment(sketch, "E88.MirrorCS", {"start": v(-14.62, -108) * mm, "end": v(-32.62, -90) * mm});
            skLineSegment(sketch, "E89.MirrorCS", {"start": v(15.38, -108) * mm, "end": v(33.38, -90) * mm});
            skCircle(sketch, "E90.MirrorC", {"center": v(0.38, -120) * mm, "radius": 6 * mm});
            skLineSegment(sketch, "E91.MirrorCS", {"start": v(0.38, -120) * mm, "end": v(0.38, -90) * mm, "construction": true});
            skArc(sketch, "E92.MirrorCS", {"start": v(15.38, -120) * mm, "mid": v(0.38, -135) * mm, "end": v(-14.62, -120) * mm});
            skLineSegment(sketch, "E93.MirrorCS", {"start": v(15.38, -120) * mm, "end": v(15.38, -108) * mm});
            skLineSegment(sketch, "E94.MirrorCS", {"start": v(-14.62, -108) * mm, "end": v(-14.62, -120) * mm});
            skSolve(sketch);
        }
        {
            var Q0;
            Q0 = qSketchRegion(id + "F16", true);
            var Q1;
            Q1=makeQuery(id+"F2.opExtrude","CAP_FACE",FACE,{"disambiguationData":[OSD([sQuery(id+"F0.wireOp",EDGE,"E12"),sQuery(id+"F0.wireOp",EDGE,"E13"),sQuery(id+"F0.wireOp",EDGE,"E14"),sQuery(id+"F0.wireOp",EDGE,"E15"),sQuery(id+"F0.wireOp",EDGE,"E17.filletArc"),sQuery(id+"F0.wireOp",EDGE,"E18.filletArc"),sQuery(id+"F0.wireOp",EDGE,"E19.filletArc"),sQuery(id+"F0.wireOp",EDGE,"E20.filletArc"),sQuery(id+"F0.wireOp",EDGE,"E25.0"),sQuery(id+"F0.wireOp",EDGE,"E25.1"),sQuery(id+"F0.wireOp",EDGE,"E25.2"),sQuery(id+"F0.wireOp",EDGE,"E25.3"),sQuery(id+"F0.wireOp",EDGE,"E25.4"),sQuery(id+"F0.wireOp",EDGE,"E25.5"),sQuery(id+"F0.wireOp",EDGE,"E25.6"),sQuery(id+"F0.wireOp",EDGE,"E25.7")])],"isStart":false});
            extrude(context, id + "F17", {"entities" : qUnion([Q0]), "endBound" : BoundingType.UP_TO_SURFACE, "endBoundEntityFace" : qUnion([Q1]), "depth" : 25 * mm});
        }
    });
